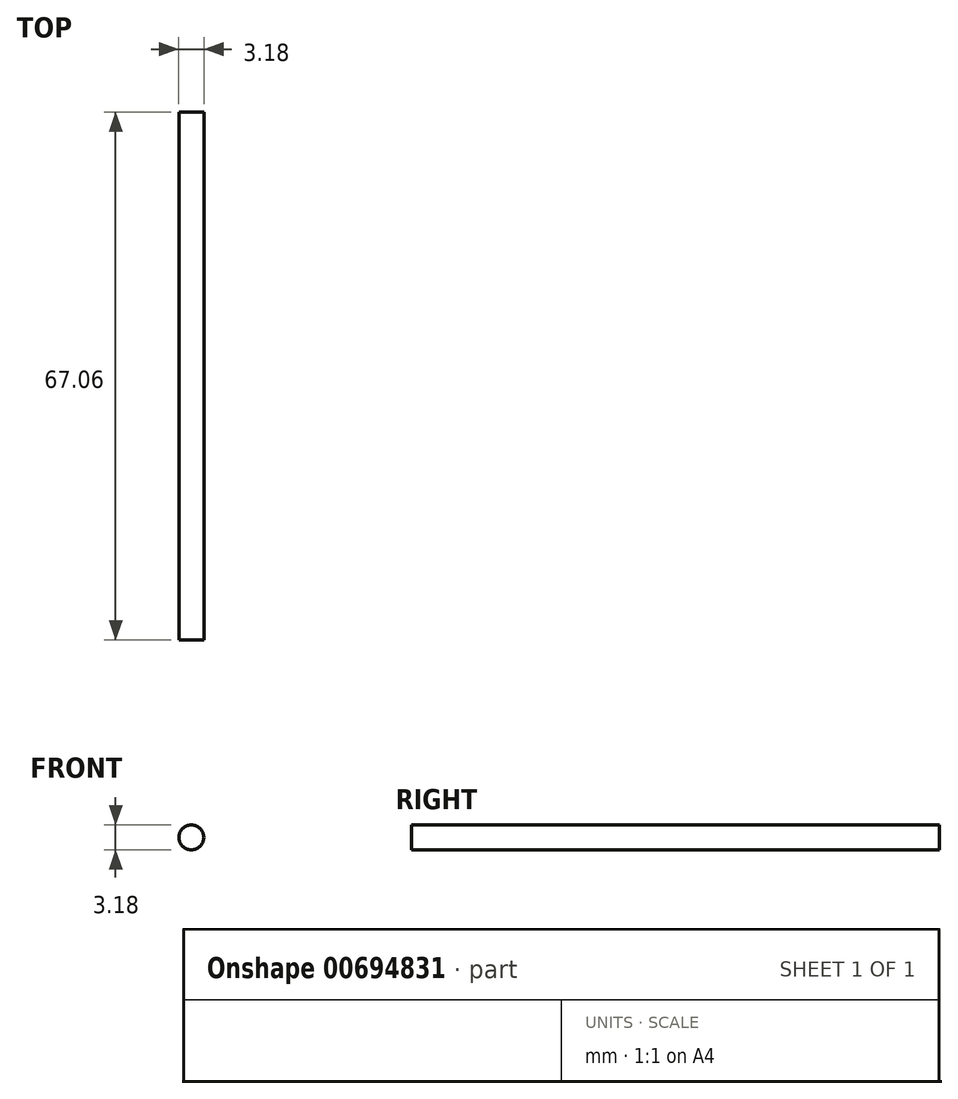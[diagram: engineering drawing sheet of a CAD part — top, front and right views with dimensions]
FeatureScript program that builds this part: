
annotation { "Feature Type Name" : "Feature", "Feature Type Description" : "" }
export const myFeature = defineFeature(function(context is Context, id is Id, definition is map)
    precondition{}
    {
        {
            var Q0;
            Q0=qCreatedBy(makeId("Front.planeOp"),FACE);
            var sketch = newSketch(context, id + "F0", { "sketchPlane" : qUnion([Q0])});
            skCircle(sketch, "E0", {"center": v(0, 0) * mm, "radius": 1.59 * mm});
            skSolve(sketch);
        }
        {
            var Q0;
            Q0=makeQuery(id+"F0.imprint","IMPRINT",FACE,{"disambiguationData":[TD([[makeQuery(id+"F0.imprint","IMPRINT",EDGE,{"derivedFrom":sQuery(id+"F0.wireOp",EDGE,"E0")}),1.0]])]});
            extrude(context, id + "F1", {"entities" : qUnion([Q0]), "depth" : 67.06 * mm, "offsetDistance" : 25.4 * mm});
        }
    });
